# Revit family: Barrier-System_TotSecSol_Baffle-Window
name_source: partatom
category: Generic Models
units: mm (PartAtom-declared; Revit-internal decimal feet)

## family parameters
Can host rebar = No
Classification Number = 23.40.70.27
Cut with Voids When Loaded = No
Host = Face
Maintain Annotation Orientation = No
Part Type = Normal
Room Calculation Point = No
Round Connector Dimension = Use Diameter
Shared = No

## types (3) — shared parameters
Assembly Code = E1010200
Construction Details = http://www.arcat.com
Default Elevation = 0' - 0"
Green Building-LEED = http://www.arcat.com
Keynote = 13 21 68
Manufacturer = Total Security Solutions
Manufacturer Fax = 517-223-0805
Manufacturer Website = http://www.tssbulletproof.com
Product Data = http://www.arcat.com
Product Properties = http://www.tssbulletproof.com
Revision = R1_2017-04
Sales Information = http://security.tssbulletproof.com
SpecWizard = http://www.arcat.com
Specification = http://www.arcat.com
Standards Conformance = as Specified
URL = http://www.tssbulletproof.com
zero-valued in all types: Expected Lifespan (Years), Maintenance Schedule (Months), Warranty Duration (Years)

## per-type parameters (varying)
| type | Description | Model |
| Level III Configuration as Specified | Total Security Solutions Level III Bullet Resistant Barrier System - Baffle Window System as Specified | Level 3 Baffle Window System as Specified |
| Level II Configuration as Specified | Total Security Solutions Level II Bullet Resistant Barrier System - Baffle Window System as Specified | Level 2 Baffle Window System as Specified |
| Level I Configuration as Specified | Total Security Solutions Level I Bullet Resistant Barrier System - Baffle Window System as Specified | Level 1 Baffle Window System as Specified |

## geometry (parser evidence)
native form markers: Sweep x1
no freeform markers — native parametric forms only
